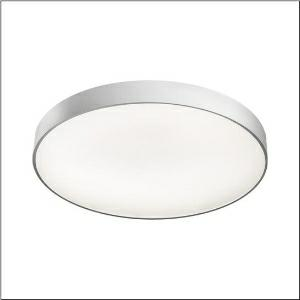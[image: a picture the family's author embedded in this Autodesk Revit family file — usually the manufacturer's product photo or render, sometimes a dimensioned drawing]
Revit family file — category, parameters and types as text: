
# Revit family: round_21_l_51mr38nd0321s
name_source: partatom
category: Lighting Fixtures
units: mm (PartAtom-declared; Revit-internal decimal feet)

## family parameters
Cut with Voids When Loaded = No
Host = Face
Light Source = No
Part Type = Normal
Room Calculation Point = No
Round Connector Dimension = Use Diameter
Shared = No

## types (1)
- Round 21 L (1 x LED, 11740 lm, 88.2 W, 3000K)
    Apparent Load = 88 VA
    CIE Flux Codes = 66 90 98 71 100
    Color Rendering = 80
    Color Temperature = 3000K
    Default Elevation = 1800 mm
    Description = Round 21 L, wall and ceiling luminaire, primary optical cover: micro prismatic cover, of PMMA, transparent, CAT 2 (L<= 3000cd/m²), light emission: direct/indirect distribution, primary light characteristic: symmetric, installation type: suspended mounting, surface-mounted, LED, rated luminous flux: 11.740lm, luminous efficacy: 133lm/W, light colour: 830, colour temperature: 3000K, control gear: DALI 2, with terminal, 5-pole, mains connection: 230V, AC, 50/60Hz, rated input power: 88.2W, housing, of aluminium, coated, silver, diameter: 850mm, height: 62mm, protection rating (complete): IP40, insulation class (complete): insulation class I (protective earthing), certification: CE, impact resistance: IK04, permissible operating ambient temperature: -10..+35°C, packaging unit: 1 piece
    Height = 87 mm
    Lamp = 1 x LED
    Lamp Light Flux = 11740 lm
    Lamp Power = 88.2 W
    Lamp count = 1
    Length = 850 mm
    Luminous efficacy = 133 lm/W
    Manufacturer = Siteco
    ModVariant = No
    Model = 51MR38ND0321S
    Mounting Place = Ceiling
    Mounting Type = Surface mounted
    Number of Poles = 1
    OnlyDefault = Yes
    Power Factor = 1
    Product Name = Round 21 L
    Product group = wall and ceiling luminaire | ceiling mounted
    ProductGroupID = 305
    Protection Class = Protection class I
    Protection Degree = IP 40
    RLX_Detail_Level = 1
    RLX_Emergency_Light_Flux = 0 lm
    RLX_Emergency_Type = 0
    RLX_Emergency_Type_DB = No
    RlxData = <blob elided: 25165 chars, md5=22a73cf0>
    Socket = socket
    Standby Power = 0 W
    System Light Flux = 11740 lm
    System Power = 88 W
    Type Comments = Product without accessories
    Type Image = l_1258322.jpg
    URL = http://relux.com
    VarID = ---
    Voltage = 0 V
    Weight = 0.00 kg
    Width = 0 mm  [stored 0 ft]

note: [stored X ft] marks values corroborated as IEEE doubles in the binary element streams (Revit-internal decimal feet)

## geometry (parser evidence)
native form markers: Blend x4, Sweep x12
no freeform markers — native parametric forms only
